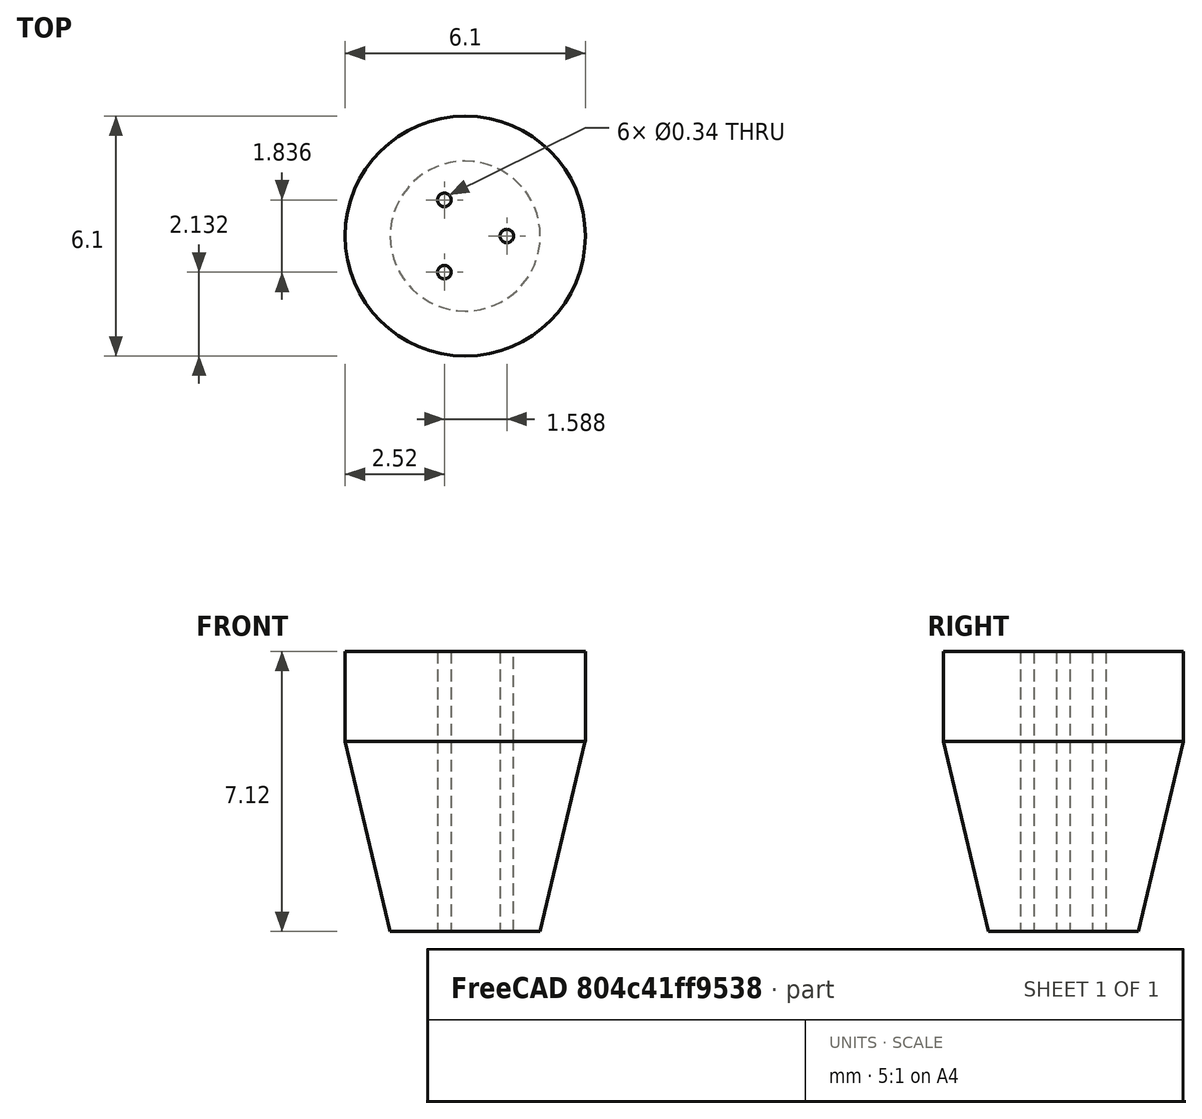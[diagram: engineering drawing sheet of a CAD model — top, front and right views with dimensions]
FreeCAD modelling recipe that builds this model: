
FCSTD DOCUMENT  (FreeCAD 0.21R0.21.2)
Label: FiberFerruleTripple
License: All rights reserved
LicenseURL: http://en.wikipedia.org/wiki/All_rights_reserved
objects: Part::Cylinder×4, Part::MultiFuse×2, Part::Compound×2, Part::Cone×1, Part::Cut×1
note: 10 computed .brp shape members not serialized (recipe doc carries the construction recipe); baked Part::Feature solids carry a one-line shape summary decoded from their .brp

FEATURE [Part::Cone] Cone
  Angle = 360
  AttacherType = Attacher::AttachEngine3D
  Height = 4.826
  Radius1 = 1.905
  Radius2 = 3.048
FEATURE [Part::Cylinder] Cylinder
  Angle = 360
  AttacherType = Attacher::AttachEngine3D
  FirstAngle = 0
  Height = 2.286
  Placement = pos=(0,0,4.83) rot=(0,0,1;0rad)
  Radius = 3.05
  SecondAngle = 0
FEATURE [Part::MultiFuse] Fusion  label="SwagelokPTFEFerrule"
  Shapes = -> [Cone,Cylinder]
FEATURE [Part::Cylinder] Cylinder001  label="Fiber0"
  Angle = 360
  AttacherType = Attacher::AttachEngine3D
  FirstAngle = 0
  Height = 7.12
  Placement = pos=(1.05833,0,0) rot=(0,0,1;0rad)
  Radius = 0.17145
  SecondAngle = 0
FEATURE [Part::Cylinder] Cylinder002  label="Fiber1"
  Angle = 360
  AttacherType = Attacher::AttachEngine3D
  FirstAngle = 0
  Height = 7.12
  Placement = pos=(1.06,0,0) rot=(0,0,1;0rad)
  Radius = 0.17145
  SecondAngle = 0
FEATURE [Part::Cylinder] Cylinder003  label="Fiber2"
  Angle = 360
  AttacherType = Attacher::AttachEngine3D
  FirstAngle = 0
  Height = 7.12
  Placement = pos=(1.06,0,0) rot=(0,0,1;0rad)
  Radius = 0.17145
  SecondAngle = 0
FEATURE [Part::Compound] Compound
  Links = -> [Cylinder003]
  Placement = pos=(0,0,0) rot=(0,0,1;2.0944rad)
FEATURE [Part::Compound] Compound001
  Links = -> [Cylinder002]
  Placement = pos=(0,0,0) rot=(0,0,1;4.18879rad)
FEATURE [Part::MultiFuse] Fusion001  label="Fibers"
  Shapes = -> [Cylinder001,Compound,Compound001]
FEATURE [Part::Cut] Cut  label="SwagelokFiberFerruleTripple0.125in"
  Base = -> Fusion
  Tool = -> Fusion001
